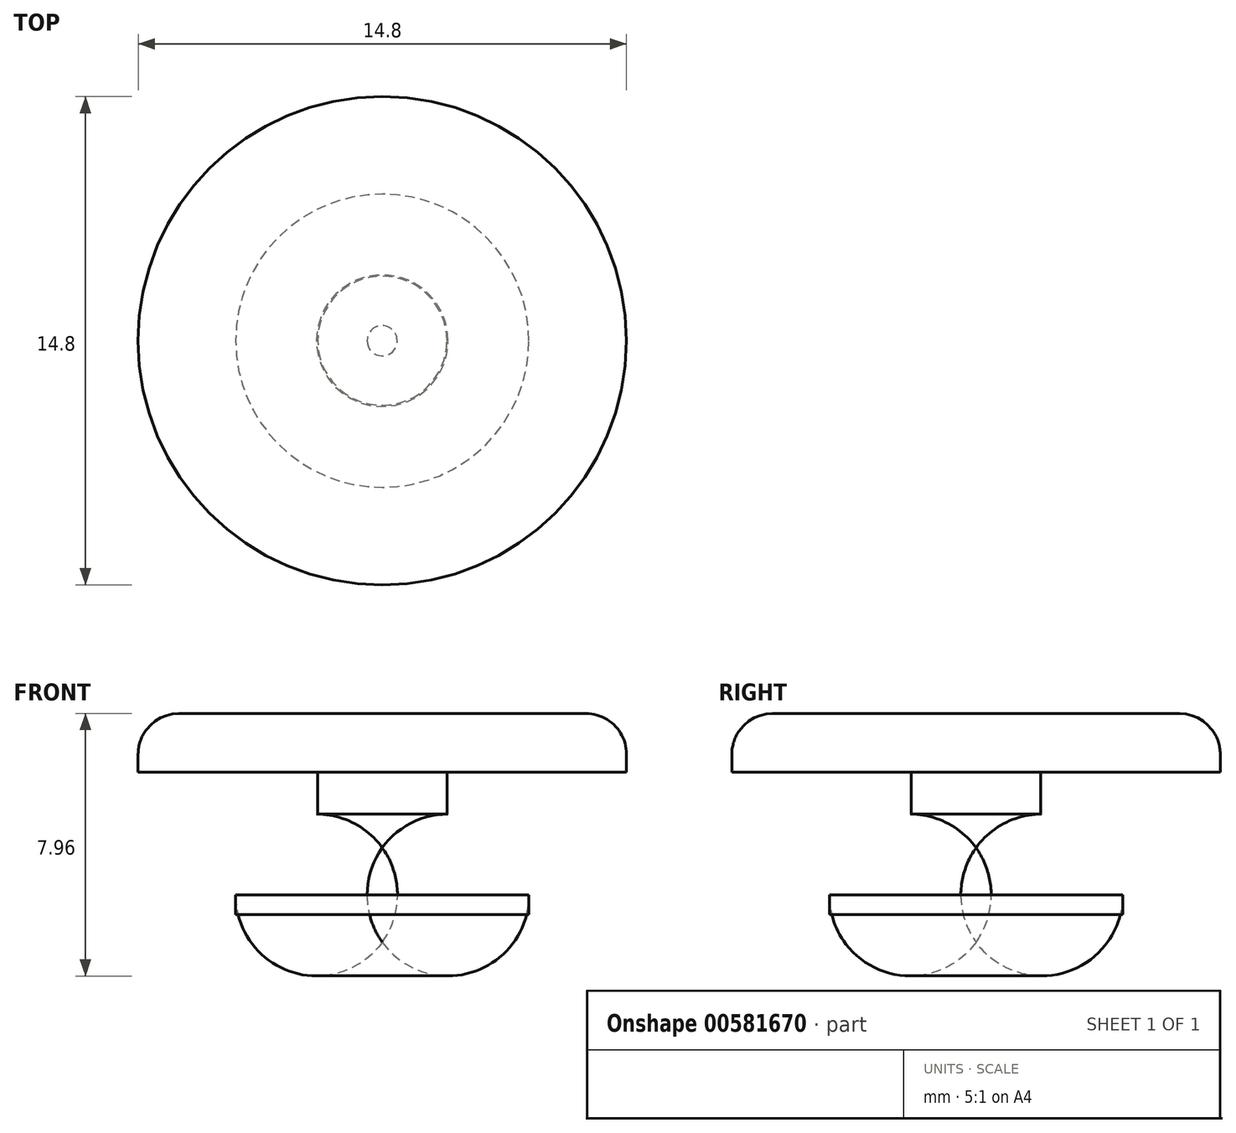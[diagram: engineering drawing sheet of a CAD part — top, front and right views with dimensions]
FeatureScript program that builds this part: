
annotation { "Feature Type Name" : "Feature", "Feature Type Description" : "" }
export const myFeature = defineFeature(function(context is Context, id is Id, definition is map)
    precondition{}
    {
        {
            var Q0;
            Q0=qCreatedBy(makeId("Top.planeOp"),FACE);
            var sketch = newSketch(context, id + "F0", { "sketchPlane" : qUnion([Q0])});
            skCircle(sketch, "E0", {"center": v(0, 0) * mm, "radius": 4.45 * mm});
            skSolve(sketch);
        }
        {
            var Q0;
            Q0 = qSketchRegion(id + "F0", true);
            extrude(context, id + "F1", {"entities" : qUnion([Q0]), "depth" : 3.05 * mm, "offsetDistance" : 25.4 * mm});
        }
        {
            var Q0;
            Q0=makeQuery(id+"F1.opExtrude","CAP_EDGE",EDGE,{"disambiguationData":[OSD([sQuery(id+"F0.wireOp",EDGE,"E0")])],"isStart":false});
            fillet(context, id + "F2", {"entities" : qUnion([Q0]), "radius" : 2.45 * mm, "tangentPropagation" : true, "allowEdgeOverflow" : false});
        }
        {
            var Q0;
            Q0=makeQuery(id+"F1.opExtrude","CAP_FACE",FACE,{"disambiguationData":[OSD([sQuery(id+"F0.wireOp",EDGE,"E0")])],"isStart":false});
            var sketch = newSketch(context, id + "F3", { "sketchPlane" : qUnion([Q0])});
            skCircle(sketch, "E1", {"center": v(0, 0) * mm, "radius": 1.96 * mm});
            skSolve(sketch);
        }
        {
            var Q0;
            Q0 = qSketchRegion(id + "F3", true);
            extrude(context, id + "F4", {"entities" : qUnion([Q0]), "operationType" : NewBodyOperationType.ADD, "depth" : 1.27 * mm, "offsetDistance" : 25.4 * mm});
        }
        {
            var Q0;
            Q0=makeQuery(id+"F4.opExtrude","CAP_FACE",FACE,{"disambiguationData":[OSD([sQuery(id+"F3.wireOp",EDGE,"E1")])],"isStart":false});
            var sketch = newSketch(context, id + "F5", { "sketchPlane" : qUnion([Q0])});
            skCircle(sketch, "E2", {"center": v(0, 0) * mm, "radius": 7.4 * mm});
            skSolve(sketch);
        }
        {
            var Q0;
            Q0 = qSketchRegion(id + "F5", true);
            extrude(context, id + "F6", {"entities" : qUnion([Q0]), "operationType" : NewBodyOperationType.ADD, "depth" : 1.78 * mm, "offsetDistance" : 25.4 * mm});
        }
        {
            var Q0;
            Q0=makeQuery(id+"F6.opExtrude","CAP_EDGE",EDGE,{"disambiguationData":[OSD([sQuery(id+"F5.wireOp",EDGE,"E2")])],"isStart":false});
            fillet(context, id + "F7", {"entities" : qUnion([Q0]), "radius" : 1.23 * mm, "tangentPropagation" : true, "allowEdgeOverflow" : false});
        }
    });
